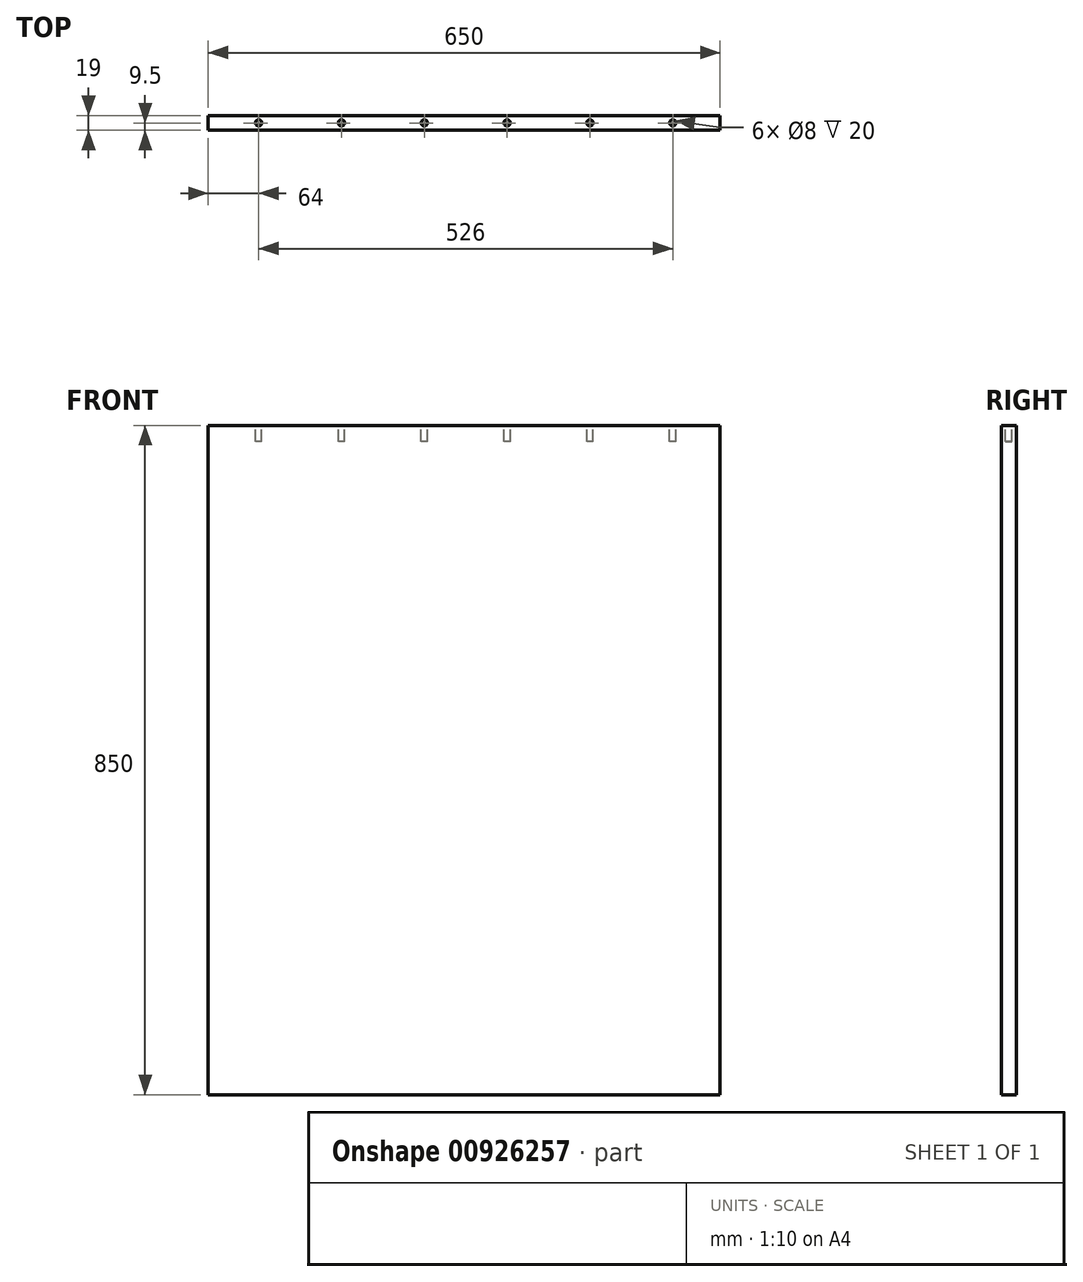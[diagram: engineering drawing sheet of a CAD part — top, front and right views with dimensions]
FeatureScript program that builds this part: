
annotation { "Feature Type Name" : "Feature", "Feature Type Description" : "" }
export const myFeature = defineFeature(function(context is Context, id is Id, definition is map)
    precondition{}
    {
        {
            var Q0;
            Q0=qCreatedBy(makeId("Front.planeOp"),FACE);
            var sketch = newSketch(context, id + "F0", { "sketchPlane" : qUnion([Q0])});
            skLineSegment(sketch, "E0.bottom", {"start": v(325, -425) * mm, "end": v(-325, -425) * mm});
            skLineSegment(sketch, "E0.top", {"start": v(325, 425) * mm, "end": v(-325, 425) * mm});
            skLineSegment(sketch, "E0.left", {"start": v(325, -425) * mm, "end": v(325, 425) * mm});
            skLineSegment(sketch, "E0.right", {"start": v(-325, -425) * mm, "end": v(-325, 425) * mm});
            skPoint(sketch, "E0.middle", {"position": v(0, 0) * mm});
            skSolve(sketch);
        }
        {
            var Q0;
            Q0=makeQuery(id+"F0.imprint","IMPRINT",FACE,{"disambiguationData":[TD([[makeQuery(id+"F0.imprint","IMPRINT",EDGE,{"derivedFrom":sQuery(id+"F0.wireOp",EDGE,"E0.bottom")}),-1.0]])]});
            extrude(context, id + "F1", {"entities" : qUnion([Q0]), "depth" : 19 * mm, "offsetDistance" : 25 * mm});
        }
        {
            var Q0;
            Q0=makeQuery(id+"F1.opExtrude","SWEPT_FACE",FACE,{"disambiguationData":[OSD([sQuery(id+"F0.wireOp",EDGE,"E0.top")])]});
            var sketch = newSketch(context, id + "F2", { "sketchPlane" : qUnion([Q0])});
            skLineSegment(sketch, "E1", {"start": v(305, 0) * mm, "end": v(305, -19) * mm, "construction": true});
            skLineSegment(sketch, "E2", {"start": v(-305, -19) * mm, "end": v(-305, 0) * mm, "construction": true});
            skLineSegment(sketch, "E3", {"start": v(305, -9.5) * mm, "end": v(-305, -9.5) * mm, "construction": true});
            skCircle(sketch, "E4", {"center": v(265, -9.5) * mm, "radius": 4 * mm});
            skCircle(sketch, "E5.1.0.0", {"center": v(159.8, -9.5) * mm, "radius": 4 * mm});
            skCircle(sketch, "E5.2.0.0", {"center": v(54.6, -9.5) * mm, "radius": 4 * mm});
            skCircle(sketch, "E5.3.0.0", {"center": v(-50.6, -9.5) * mm, "radius": 4 * mm});
            skCircle(sketch, "E5.4.0.0", {"center": v(-155.8, -9.5) * mm, "radius": 4 * mm});
            skCircle(sketch, "E5.5.0.0", {"center": v(-261, -9.5) * mm, "radius": 4 * mm});
            skLineSegment(sketch, "E5.direction1", {"start": v(265, -9.5) * mm, "end": v(159.8, -9.5) * mm, "construction": true});
            skSolve(sketch);
        }
        {
            var Q0;
            Q0=makeQuery(id+"F2.imprint","IMPRINT",FACE,{"disambiguationData":[TD([[makeQuery(id+"F2.imprint","IMPRINT",EDGE,{"derivedFrom":sQuery(id+"F2.wireOp",EDGE,"E4")}),1.0]])]});
            var Q1;
            Q1=makeQuery(id+"F2.imprint","IMPRINT",FACE,{"disambiguationData":[TD([[makeQuery(id+"F2.imprint","IMPRINT",EDGE,{"derivedFrom":sQuery(id+"F2.wireOp",EDGE,"E5.1.0.0")}),1.0]])]});
            var Q2;
            Q2=makeQuery(id+"F2.imprint","IMPRINT",FACE,{"disambiguationData":[TD([[makeQuery(id+"F2.imprint","IMPRINT",EDGE,{"derivedFrom":sQuery(id+"F2.wireOp",EDGE,"E5.2.0.0")}),1.0]])]});
            var Q3;
            Q3=makeQuery(id+"F2.imprint","IMPRINT",FACE,{"disambiguationData":[TD([[makeQuery(id+"F2.imprint","IMPRINT",EDGE,{"derivedFrom":sQuery(id+"F2.wireOp",EDGE,"E5.3.0.0")}),1.0]])]});
            var Q4;
            Q4=makeQuery(id+"F2.imprint","IMPRINT",FACE,{"disambiguationData":[TD([[makeQuery(id+"F2.imprint","IMPRINT",EDGE,{"derivedFrom":sQuery(id+"F2.wireOp",EDGE,"E5.4.0.0")}),1.0]])]});
            var Q5;
            Q5=makeQuery(id+"F2.imprint","IMPRINT",FACE,{"disambiguationData":[TD([[makeQuery(id+"F2.imprint","IMPRINT",EDGE,{"derivedFrom":sQuery(id+"F2.wireOp",EDGE,"E5.5.0.0")}),1.0]])]});
            extrude(context, id + "F3", {"entities" : qUnion([Q0, Q1, Q2, Q3, Q4, Q5]), "operationType" : NewBodyOperationType.REMOVE, "oppositeDirection" : true, "depth" : 20 * mm, "offsetDistance" : 25 * mm});
        }
    });
